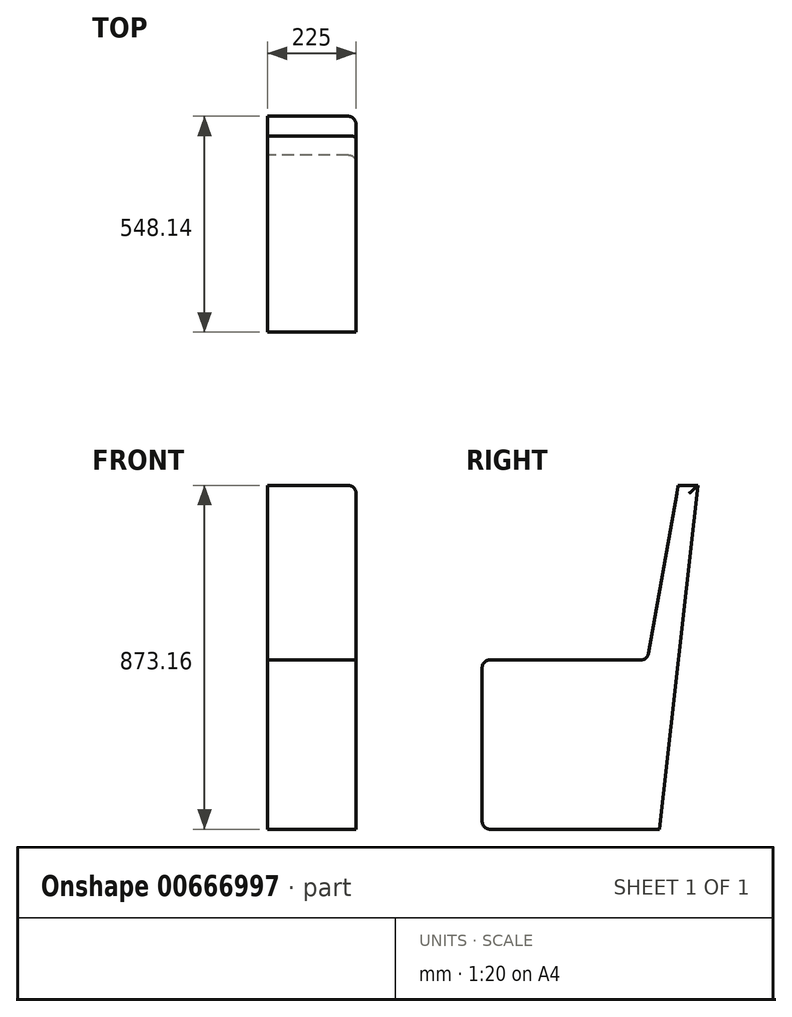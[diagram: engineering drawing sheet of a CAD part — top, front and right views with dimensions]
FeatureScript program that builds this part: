
annotation { "Feature Type Name" : "Feature", "Feature Type Description" : "" }
export const myFeature = defineFeature(function(context is Context, id is Id, definition is map)
    precondition{}
    {
        {
            var Q0;
            Q0=qCreatedBy(makeId("Right.planeOp"),FACE);
            var sketch = newSketch(context, id + "F0", { "sketchPlane" : qUnion([Q0])});
            skLineSegment(sketch, "E0", {"start": v(0, 0) * mm, "end": v(-450, 0) * mm});
            skLineSegment(sketch, "E1", {"start": v(-450, 430) * mm, "end": v(-30, 430) * mm});
            skLineSegment(sketch, "E2", {"start": v(-30, 430) * mm, "end": v(48.14, 873.16) * mm});
            skLineSegment(sketch, "E3", {"start": v(48.14, 873.16) * mm, "end": v(98.14, 873.16) * mm});
            skLineSegment(sketch, "E4", {"start": v(98.14, 873.16) * mm, "end": v(0, 0) * mm});
            skLineSegment(sketch, "E5", {"start": v(-450, 430) * mm, "end": v(-450, 0) * mm});
            skSolve(sketch);
        }
        {
            var Q0;
            Q0=makeQuery(id+"F0.imprint","IMPRINT",FACE,{"disambiguationData":[TD([[makeQuery(id+"F0.imprint","IMPRINT",EDGE,{"derivedFrom":sQuery(id+"F0.wireOp",EDGE,"E0")}),-1.0]])]});
            extrude(context, id + "F1", {"entities" : qUnion([Q0]), "depth" : 225 * mm, "offsetDistance" : 25 * mm});
        }
        {
            var Q0;
            Q0=makeQuery(id+"F1.opExtrude","SWEPT_EDGE",EDGE,{"disambiguationData":[OSD([sQuery(id+"F0.wireOp",EDGE,"E1"),sQuery(id+"F0.wireOp",EDGE,"E5")])]});
            var Q1;
            Q1=makeQuery(id+"F1.opExtrude","SWEPT_EDGE",EDGE,{"disambiguationData":[OSD([sQuery(id+"F0.wireOp",EDGE,"E1"),sQuery(id+"F0.wireOp",EDGE,"E2")])]});
            var Q2;
            Q2=makeQuery(id+"F1.opExtrude","SWEPT_EDGE",EDGE,{"disambiguationData":[OSD([sQuery(id+"F0.wireOp",EDGE,"E0"),sQuery(id+"F0.wireOp",EDGE,"E5")])]});
            var Q3;
            Q3=makeQuery(id+"F1.opExtrude","CAP_EDGE",EDGE,{"disambiguationData":[OSD([sQuery(id+"F0.wireOp",EDGE,"E3")])],"isStart":false});
            var Q4;
            Q4=makeQuery(id+"F1.opExtrude","CAP_EDGE",EDGE,{"disambiguationData":[OSD([sQuery(id+"F0.wireOp",EDGE,"E4")])],"isStart":false});
            fillet(context, id + "F2", {"entities" : qUnion([Q0, Q1, Q2, Q3, Q4]), "radius" : 20 * mm, "tangentPropagation" : true, "allowEdgeOverflow" : false});
        }
    });
